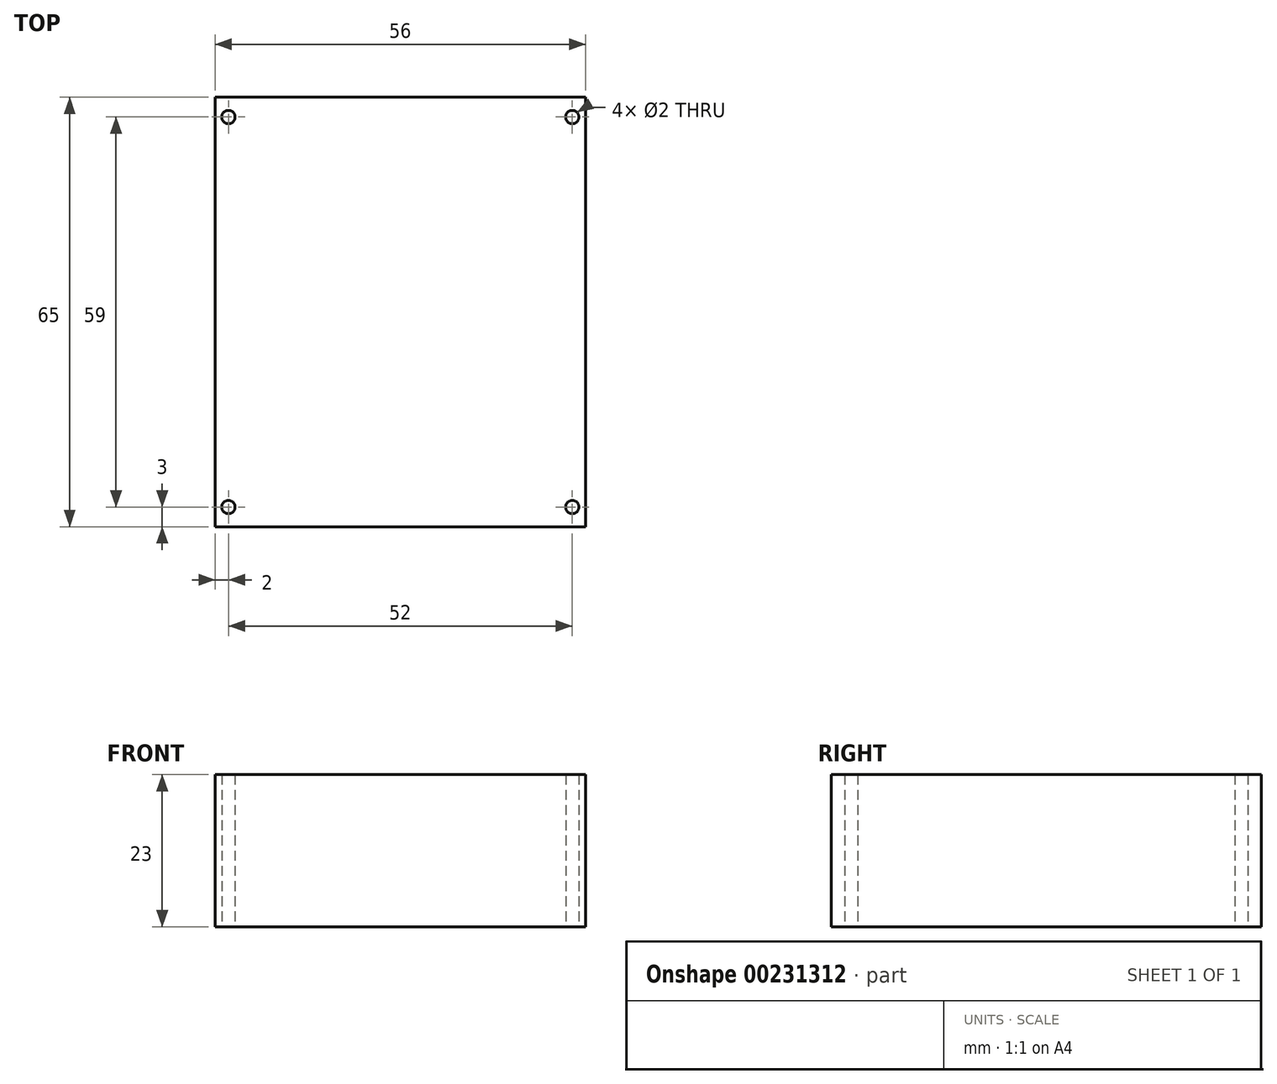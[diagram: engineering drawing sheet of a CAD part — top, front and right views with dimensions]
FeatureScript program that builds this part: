
annotation { "Feature Type Name" : "Feature", "Feature Type Description" : "" }
export const myFeature = defineFeature(function(context is Context, id is Id, definition is map)
    precondition{}
    {
        {
            var Q0;
            Q0=qCreatedBy(makeId("Top.planeOp"),FACE);
            var sketch = newSketch(context, id + "F0", { "sketchPlane" : qUnion([Q0])});
            skLineSegment(sketch, "E0.bottom", {"start": v(-50.31, 48.02) * mm, "end": v(5.69, 48.02) * mm});
            skLineSegment(sketch, "E0.top", {"start": v(-50.31, -16.98) * mm, "end": v(5.69, -16.98) * mm});
            skLineSegment(sketch, "E0.left", {"start": v(-50.31, 48.02) * mm, "end": v(-50.31, -16.98) * mm});
            skLineSegment(sketch, "E0.right", {"start": v(5.69, 48.02) * mm, "end": v(5.69, -16.98) * mm});
            skCircle(sketch, "E1", {"center": v(-48.31, 45.02) * mm, "radius": 1 * mm});
            skCircle(sketch, "E2", {"center": v(-48.31, -13.98) * mm, "radius": 1 * mm});
            skCircle(sketch, "E3", {"center": v(3.69, 45.02) * mm, "radius": 1 * mm});
            skCircle(sketch, "E4", {"center": v(3.69, -13.98) * mm, "radius": 1 * mm});
            skSolve(sketch);
        }
        {
            var Q0;
            Q0=makeQuery(id+"F0.imprint","IMPRINT",FACE,{"disambiguationData":[TD([[makeQuery(id+"F0.imprint","IMPRINT",EDGE,{"derivedFrom":sQuery(id+"F0.wireOp",EDGE,"E0.bottom")}),-1.0]])]});
            extrude(context, id + "F1", {"entities" : qUnion([Q0]), "depth" : 23 * mm});
        }
    });
